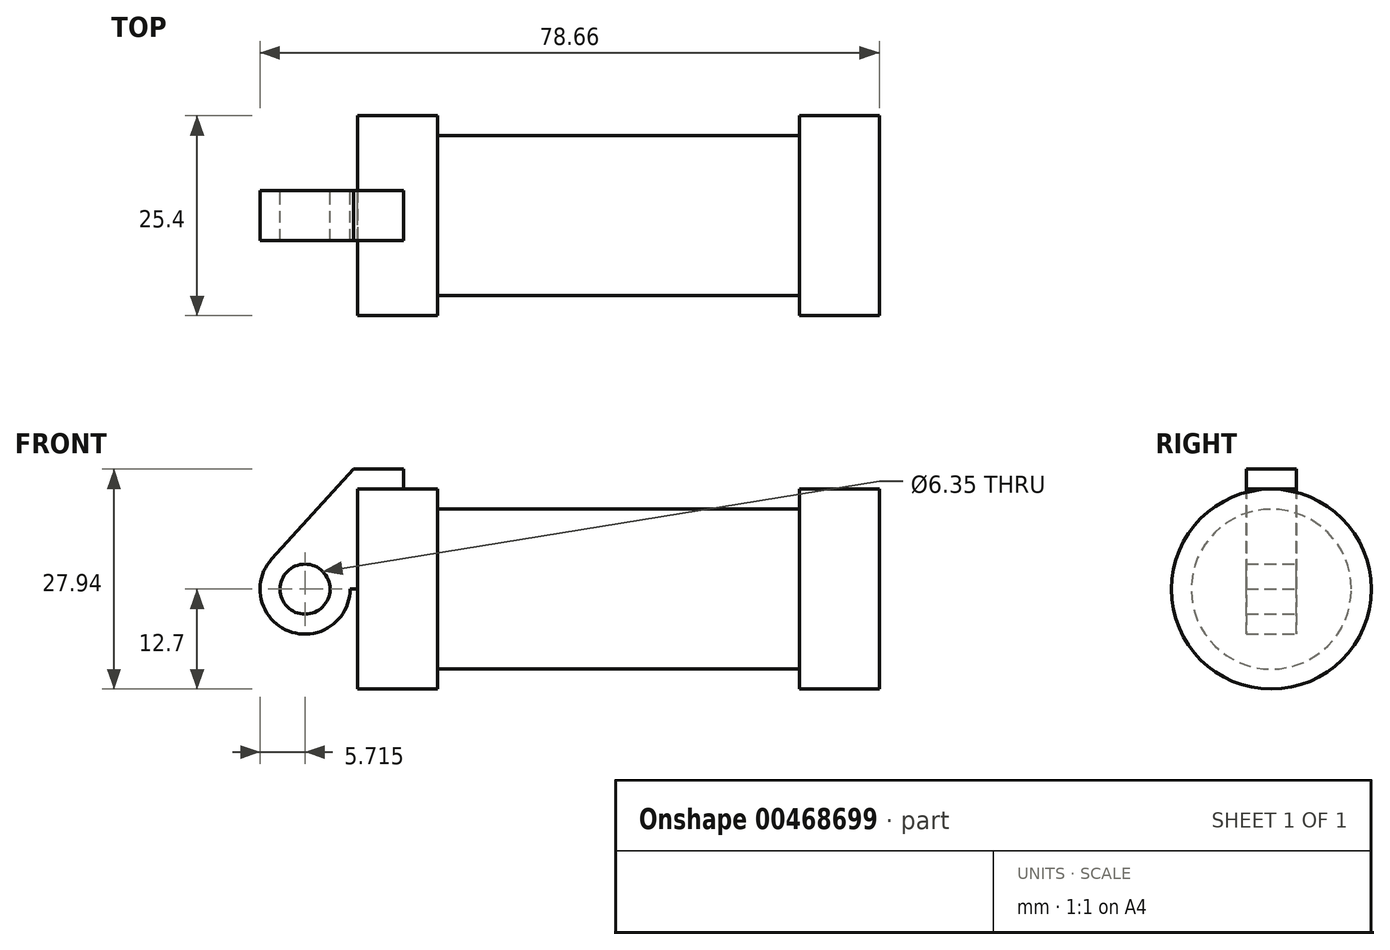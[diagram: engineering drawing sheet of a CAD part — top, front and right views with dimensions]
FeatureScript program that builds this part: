
annotation { "Feature Type Name" : "Feature", "Feature Type Description" : "" }
export const myFeature = defineFeature(function(context is Context, id is Id, definition is map)
    precondition{}
    {
        {
            var Q0;
            Q0=qCreatedBy(makeId("Front.planeOp"),FACE);
            var sketch = newSketch(context, id + "F0", { "sketchPlane" : qUnion([Q0])});
            skLineSegment(sketch, "E0", {"start": v(0, 0) * mm, "end": v(0, 12.7) * mm});
            skLineSegment(sketch, "E1", {"start": v(0, 12.7) * mm, "end": v(10.16, 12.7) * mm});
            skLineSegment(sketch, "E2", {"start": v(10.16, 12.7) * mm, "end": v(10.16, 10.16) * mm});
            skLineSegment(sketch, "E3", {"start": v(10.16, 10.16) * mm, "end": v(56.13, 10.16) * mm});
            skLineSegment(sketch, "E4", {"start": v(56.13, 10.16) * mm, "end": v(56.13, 12.7) * mm});
            skLineSegment(sketch, "E5", {"start": v(56.13, 12.7) * mm, "end": v(66.3, 12.7) * mm});
            skLineSegment(sketch, "E6", {"start": v(66.3, 12.7) * mm, "end": v(66.3, 0) * mm});
            skLineSegment(sketch, "E7", {"start": v(66.3, 0) * mm, "end": v(0, 0) * mm});
            skLineSegment(sketch, "E8", {"start": v(5.84, 15.24) * mm, "end": v(-0.5, 15.24) * mm});
            skLineSegment(sketch, "E9", {"start": v(-0.5, 15.24) * mm, "end": v(-10.88, 3.85) * mm});
            skLineSegment(sketch, "E10", {"start": v(0, 0) * mm, "end": v(-6.65, 0) * mm});
            skCircle(sketch, "E11", {"center": v(-6.65, 0) * mm, "radius": 5.72 * mm});
            skCircle(sketch, "E12", {"center": v(-6.65, 0) * mm, "radius": 3.18 * mm});
            skLineSegment(sketch, "E13", {"start": v(5.84, 15.24) * mm, "end": v(5.84, -9.4) * mm});
            skLineSegment(sketch, "E14", {"start": v(5.84, -9.4) * mm, "end": v(-8.18, -5.5) * mm});
            skSolve(sketch);
        }
        {
            var Q0;
            {var subQ0=sQuery(id+"F0.wireOp",EDGE,"E2");Q0=makeQuery(id+"F0.imprint","IMPRINT",FACE,{"disambiguationData":[TD([[makeQuery(id+"F0.imprint","IMPRINT",EDGE,{"derivedFrom":subQ0}),-1.0]])]});}
            var Q1;
            {var subQ0=sQuery(id+"F0.wireOp",EDGE,"E0");Q1=makeQuery(id+"F0.imprint","IMPRINT",FACE,{"disambiguationData":[TD([[makeQuery(id+"F0.imprint","IMPRINT",EDGE,{"derivedFrom":subQ0}),-1.0]])]});}
            var Q2;
            Q2=sQuery(id+"F0.wireOp",EDGE,"E7");
            revolve(context, id + "F1", {"entities" : qUnion([Q0, Q1]), "axis" : qUnion([Q2]), "revolveType" : RevolveType.FULL});
        }
        {
            var Q0;
            {var subQ1=sQuery(id+"F0.wireOp",EDGE,"E0");Q0=makeQuery(id+"F0.imprint","IMPRINT",FACE,{"disambiguationData":[TD([[makeQuery(id+"F0.imprint","IMPRINT",EDGE,{"derivedFrom":subQ1}),1.0]])]});}
            var Q1;
            {var subQ5=sQuery(id+"F0.wireOp",EDGE,"E12");Q1=makeQuery(id+"F0.imprint","IMPRINT",FACE,{"disambiguationData":[TD([[makeQuery(id+"F0.imprint","IMPRINT",EDGE,{"derivedFrom":subQ5}),-1.0]])]});}
            extrude(context, id + "F2", {"entities" : qUnion([Q0, Q1]), "depth" : 3.17 * mm, "hasSecondDirection" : true, "secondDirectionOppositeDirection" : true, "secondDirectionDepth" : 3.17 * mm});
        }
    });
